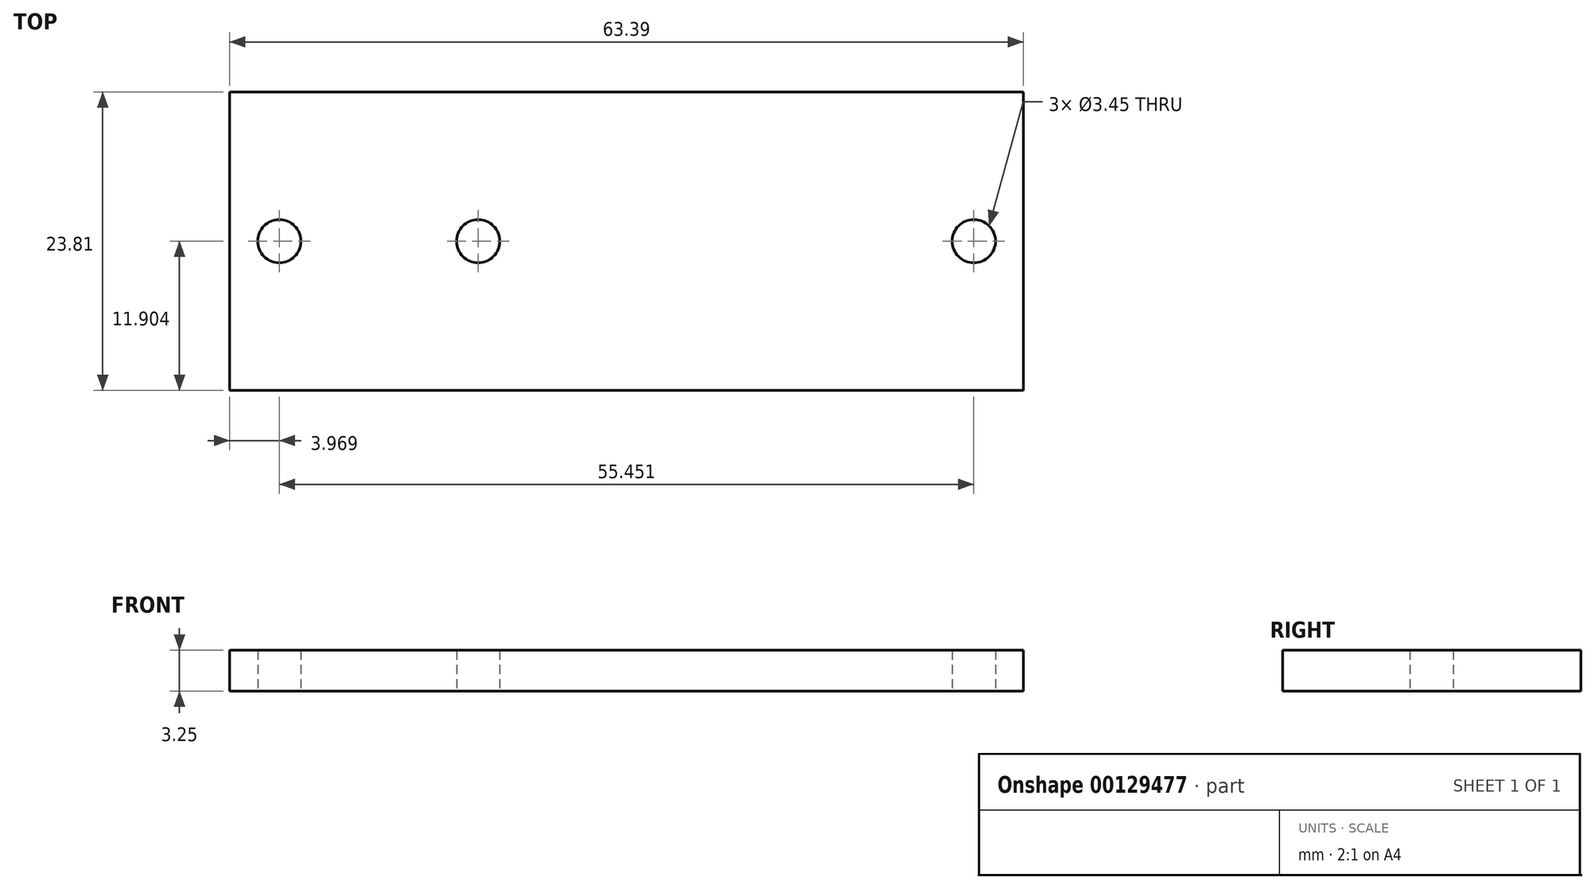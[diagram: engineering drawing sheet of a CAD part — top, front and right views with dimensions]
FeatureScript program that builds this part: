
annotation { "Feature Type Name" : "Feature", "Feature Type Description" : "" }
export const myFeature = defineFeature(function(context is Context, id is Id, definition is map)
    precondition{}
    {
        {
            var Q0;
            Q0=qCreatedBy(makeId("Top.planeOp"),FACE);
            var sketch = newSketch(context, id + "F0", { "sketchPlane" : qUnion([Q0])});
            skLineSegment(sketch, "E0.bottom", {"start": v(0, 0) * mm, "end": v(63.39, 0) * mm});
            skLineSegment(sketch, "E0.top", {"start": v(0, -23.81) * mm, "end": v(63.39, -23.81) * mm});
            skLineSegment(sketch, "E0.left", {"start": v(0, 0) * mm, "end": v(0, -23.81) * mm});
            skLineSegment(sketch, "E0.right", {"start": v(63.39, 0) * mm, "end": v(63.39, -23.81) * mm});
            skLineSegment(sketch, "E1", {"start": v(63.39, -11.9) * mm, "end": v(59.42, -11.9) * mm});
            skLineSegment(sketch, "E2", {"start": v(0, -11.9) * mm, "end": v(3.97, -11.9) * mm});
            skLineSegment(sketch, "E3", {"start": v(3.97, -11.9) * mm, "end": v(19.84, -11.9) * mm});
            skCircle(sketch, "E4", {"center": v(3.97, -11.9) * mm, "radius": 1.73 * mm});
            skCircle(sketch, "E5", {"center": v(19.84, -11.9) * mm, "radius": 1.73 * mm});
            skCircle(sketch, "E6", {"center": v(59.42, -11.9) * mm, "radius": 1.73 * mm});
            skSolve(sketch);
        }
        {
            var Q0;
            Q0=qSketchRegion(id+"F0",true);
            extrude(context, id + "F1", {"entities" : qUnion([Q0]), "depth" : 3.25 * mm});
        }
    });
